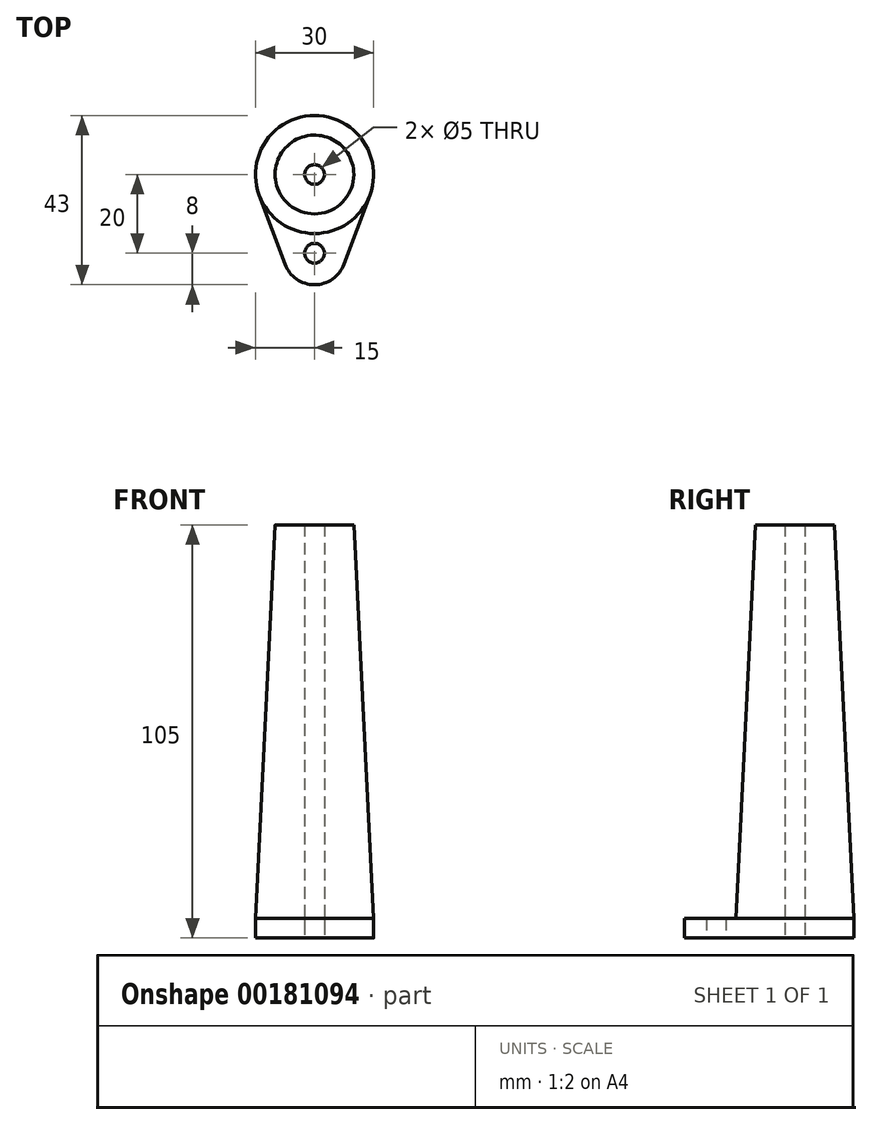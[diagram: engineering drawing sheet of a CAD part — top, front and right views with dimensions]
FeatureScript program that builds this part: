
annotation { "Feature Type Name" : "Feature", "Feature Type Description" : "" }
export const myFeature = defineFeature(function(context is Context, id is Id, definition is map)
    precondition{}
    {
        {
            var Q0;
            Q0=qCreatedBy(makeId("Top.planeOp"),FACE);
            var sketch = newSketch(context, id + "F0", { "sketchPlane" : qUnion([Q0])});
            skCircle(sketch, "E0", {"center": v(0, 0) * mm, "radius": 2.5 * mm});
            skCircle(sketch, "E1", {"center": v(0, -20) * mm, "radius": 2.5 * mm});
            skArc(sketch, "E2", {"start": v(14.05, -5.25) * mm, "mid": v(0, 15) * mm, "end": v(-14.05, -5.25) * mm});
            skArc(sketch, "E3", {"start": v(-7.5, -22.8) * mm, "mid": v(0, -28) * mm, "end": v(7.5, -22.8) * mm});
            skLineSegment(sketch, "E4", {"start": v(-14.05, -5.25) * mm, "end": v(-7.5, -22.8) * mm});
            skLineSegment(sketch, "E5", {"start": v(7.5, -22.8) * mm, "end": v(14.05, -5.25) * mm});
            skSolve(sketch);
        }
        {
            var Q0;
            Q0 = qSketchRegion(id + "F0", true);
            extrude(context, id + "F1", {"entities" : qUnion([Q0]), "depth" : 5 * mm});
        }
        {
            var Q0;
            Q0=makeQuery(id+"F1.opExtrude","CAP_FACE",FACE,{"disambiguationData":[OSD([sQuery(id+"F0.wireOp",EDGE,"E0"),sQuery(id+"F0.wireOp",EDGE,"E1"),sQuery(id+"F0.wireOp",EDGE,"E2"),sQuery(id+"F0.wireOp",EDGE,"E3"),sQuery(id+"F0.wireOp",EDGE,"E4"),sQuery(id+"F0.wireOp",EDGE,"E5")])],"isStart":false});
            var sketch = newSketch(context, id + "F2", { "sketchPlane" : qUnion([Q0])});
            skCircle(sketch, "E6", {"center": v(0, 0) * mm, "radius": 15 * mm});
            skCircle(sketch, "E7.0", {"center": v(0, 0) * mm, "radius": 2.5 * mm});
            skSolve(sketch);
        }
        {
            var Q0;
            Q0 = qSketchRegion(id + "F2", true);
            extrude(context, id + "F3", {"entities" : qUnion([Q0]), "operationType" : NewBodyOperationType.ADD, "depth" : 100 * mm});
        }
        {
            var Q0;
            Q0=makeQuery(id+"F3.opExtrude","CAP_EDGE",EDGE,{"disambiguationData":[OSD([sQuery(id+"F2.wireOp",EDGE,"E6")])],"isStart":false});
            chamfer(context, id + "F4", {"entities" : qUnion([Q0]), "chamferType" : ChamferType.TWO_OFFSETS, "width1" : 5 * mm, "oppositeDirection" : false, "width2" : 100 * mm, "tangentPropagation" : true});
        }
    });
